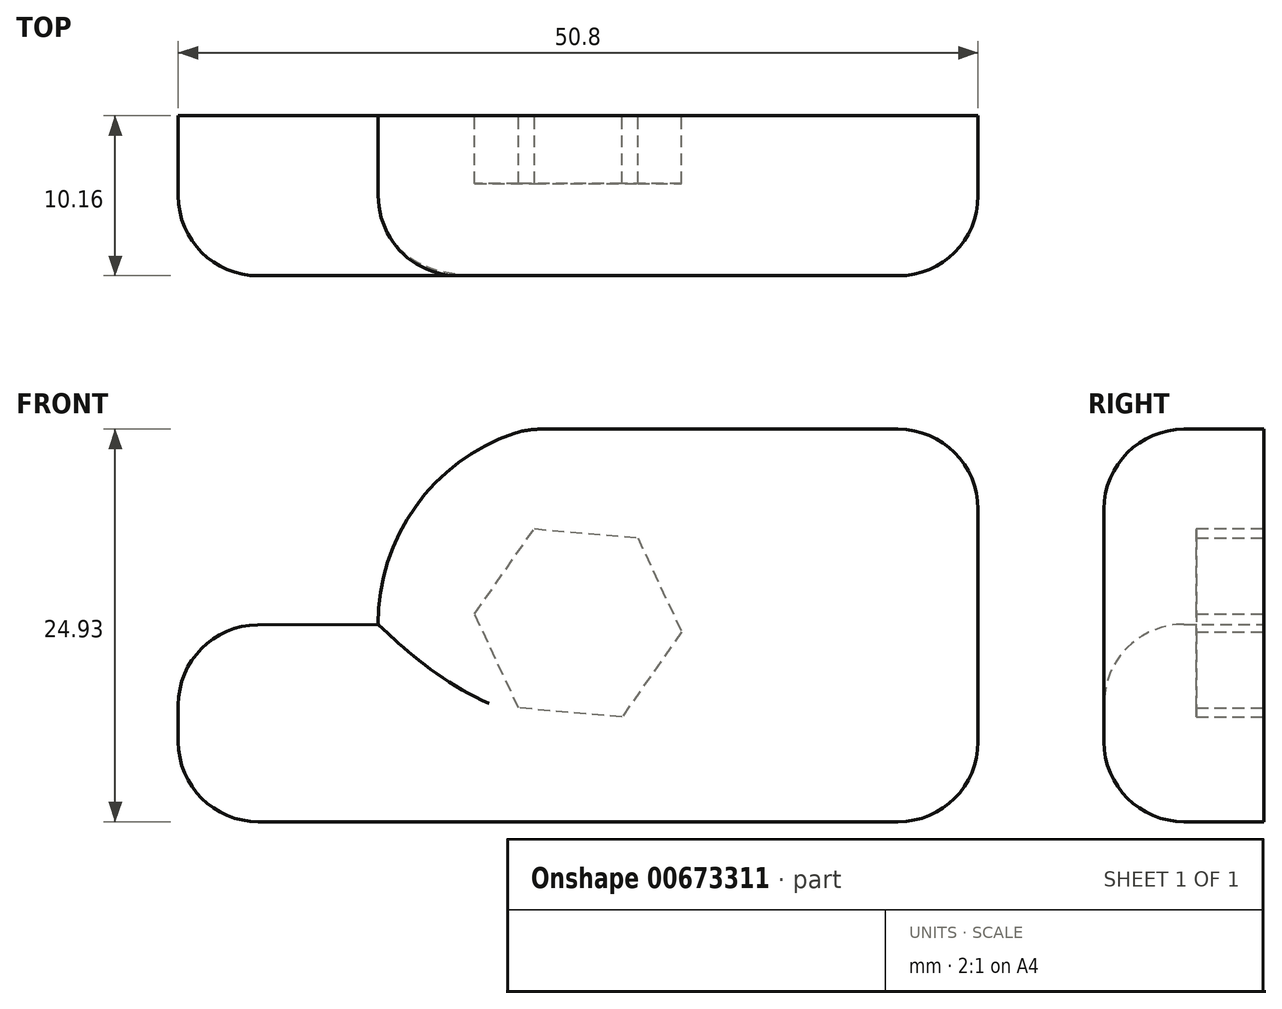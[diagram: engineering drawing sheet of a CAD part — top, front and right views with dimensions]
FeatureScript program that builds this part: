
annotation { "Feature Type Name" : "Feature", "Feature Type Description" : "" }
export const myFeature = defineFeature(function(context is Context, id is Id, definition is map)
    precondition{}
    {
        {
            var Q0;
            Q0=qCreatedBy(makeId("Front.planeOp"),FACE);
            var sketch = newSketch(context, id + "F0", { "sketchPlane" : qUnion([Q0])});
            skCircle(sketch, "E0.cCircle", {"center": v(0, 0) * mm, "radius": 5.72 * mm, "construction": true});
            skLineSegment(sketch, "E0.0", {"start": v(3.79, 5.4) * mm, "end": v(6.57, -0.58) * mm});
            skLineSegment(sketch, "E0.1", {"start": v(6.57, -0.58) * mm, "end": v(2.79, -5.98) * mm});
            skLineSegment(sketch, "E0.2", {"start": v(2.79, -5.98) * mm, "end": v(-3.79, -5.4) * mm});
            skLineSegment(sketch, "E0.3", {"start": v(-3.79, -5.4) * mm, "end": v(-6.57, 0.58) * mm});
            skLineSegment(sketch, "E0.4", {"start": v(-6.57, 0.58) * mm, "end": v(-2.79, 5.98) * mm});
            skLineSegment(sketch, "E0.5", {"start": v(-2.79, 5.98) * mm, "end": v(3.79, 5.4) * mm});
            skPoint(sketch, "E0.0.midPoint", {"position": v(5.18, 2.41) * mm});
            skCircle(sketch, "E1", {"center": v(0, 0) * mm, "radius": 12.7 * mm});
            skLineSegment(sketch, "E2.bottom", {"start": v(-25.4, 12.3) * mm, "end": v(25.4, 12.3) * mm});
            skLineSegment(sketch, "E2.top", {"start": v(-25.4, -12.63) * mm, "end": v(25.4, -12.63) * mm});
            skLineSegment(sketch, "E2.left", {"start": v(-25.4, 12.3) * mm, "end": v(-25.4, -12.63) * mm});
            skLineSegment(sketch, "E2.right", {"start": v(25.4, 12.3) * mm, "end": v(25.4, -12.63) * mm});
            skLineSegment(sketch, "E3", {"start": v(-25.4, -0.17) * mm, "end": v(0, 0) * mm});
            skSolve(sketch);
        }
        {
            var Q0;
            {var subQ0=sQuery(id+"F0.wireOp",EDGE,"E3");var subQ1=sQuery(id+"F0.wireOp",EDGE,"E1");var subQ2=makeQuery(id+"F0.imprint","INTERSECT",VERTEX,{"derivedFrom":[subQ1,subQ0]});Q0=makeQuery(id+"F0.imprint","IMPRINT",FACE,{"disambiguationData":[TD([[makeQuery(id+"F0.imprint","IMPRINT",EDGE,{"disambiguationData":[TD([[subQ2,-1.0]])],"derivedFrom":subQ1}),-1.0]])]});}
            var Q1;
            {var subQ0=sQuery(id+"F0.wireOp",EDGE,"E2.bottom");var subQ1=sQuery(id+"F0.wireOp",EDGE,"E1");var subQ2=makeQuery(id+"F0.imprint","INTERSECT",VERTEX,{"disambiguationData":[OD(0.0)],"derivedFrom":[subQ1,subQ0]});Q1=makeQuery(id+"F0.imprint","IMPRINT",FACE,{"disambiguationData":[TD([[makeQuery(id+"F0.imprint","IMPRINT",EDGE,{"disambiguationData":[TD([[subQ2,-1.0]])],"derivedFrom":subQ1}),-1.0]])]});}
            var Q2;
            {var subQ5=sQuery(id+"F0.wireOp",EDGE,"E2.right");Q2=makeQuery(id+"F0.imprint","IMPRINT",FACE,{"disambiguationData":[TD([[makeQuery(id+"F0.imprint","IMPRINT",EDGE,{"derivedFrom":subQ5}),-1.0]])]});}
            var Q3;
            Q3=makeQuery(id+"F0.imprint","IMPRINT",FACE,{"disambiguationData":[TD([[makeQuery(id+"F0.imprint","IMPRINT",EDGE,{"derivedFrom":sQuery(id+"F0.wireOp",EDGE,"E0.0")}),1.0]])]});
            var Q4;
            Q4=makeQuery(id+"F0.imprint","IMPRINT",FACE,{"disambiguationData":[TD([[makeQuery(id+"F0.imprint","IMPRINT",EDGE,{"derivedFrom":sQuery(id+"F0.wireOp",EDGE,"E0.0")}),-1.0]])]});
            var Q5;
            {var subQ0=sQuery(id+"F0.wireOp",EDGE,"E2.top");var subQ1=sQuery(id+"F0.wireOp",EDGE,"E1");var subQ2=makeQuery(id+"F0.imprint","INTERSECT",VERTEX,{"disambiguationData":[OD(0.0)],"derivedFrom":[subQ1,subQ0]});Q5=makeQuery(id+"F0.imprint","IMPRINT",FACE,{"disambiguationData":[TD([[makeQuery(id+"F0.imprint","IMPRINT",EDGE,{"disambiguationData":[TD([[subQ2,-1.0]])],"derivedFrom":subQ1}),1.0]])]});}
            var Q6;
            {var subQ0=sQuery(id+"F0.wireOp",EDGE,"E2.bottom");var subQ1=sQuery(id+"F0.wireOp",EDGE,"E1");var subQ2=makeQuery(id+"F0.imprint","INTERSECT",VERTEX,{"disambiguationData":[OD(0.0)],"derivedFrom":[subQ1,subQ0]});Q6=makeQuery(id+"F0.imprint","IMPRINT",FACE,{"disambiguationData":[TD([[makeQuery(id+"F0.imprint","IMPRINT",EDGE,{"disambiguationData":[TD([[subQ2,1.0]])],"derivedFrom":subQ1}),1.0]])]});}
            extrude(context, id + "F1", {"entities" : qUnion([Q0, Q1, Q2, Q3, Q4, Q5, Q6]), "depth" : 10.16 * mm, "offsetDistance" : 25.4 * mm});
        }
        {
            var Q0;
            Q0=makeQuery(id+"F0.imprint","IMPRINT",FACE,{"disambiguationData":[TD([[makeQuery(id+"F0.imprint","IMPRINT",EDGE,{"derivedFrom":sQuery(id+"F0.wireOp",EDGE,"E0.0")}),-1.0]])]});
            extrude(context, id + "F2", {"entities" : qUnion([Q0]), "operationType" : NewBodyOperationType.REMOVE, "depth" : 4.3 * mm, "offsetDistance" : 25.4 * mm});
        }
        {
            var Q0;
            Q0=makeQuery(id+"F1.opExtrude","SWEPT_EDGE",EDGE,{"disambiguationData":[OSD([sQuery(id+"F0.wireOp",EDGE,"E2.bottom"),sQuery(id+"F0.wireOp",EDGE,"E2.left")])]});
            var Q1;
            Q1=makeQuery(id+"F1.opExtrude","SWEPT_EDGE",EDGE,{"disambiguationData":[OSD([sQuery(id+"F0.wireOp",EDGE,"E2.bottom"),sQuery(id+"F0.wireOp",EDGE,"E2.right")])]});
            var Q2;
            Q2=makeQuery(id+"F1.opExtrude","SWEPT_EDGE",EDGE,{"disambiguationData":[OSD([sQuery(id+"F0.wireOp",EDGE,"E2.top"),sQuery(id+"F0.wireOp",EDGE,"E2.right")])]});
            var Q3;
            {var subQ0=sQuery(id+"F0.wireOp",EDGE,"E2.top");Q3=makeQuery(id+"F1.opExtrude","CAP_EDGE",EDGE,{"disambiguationData":[OSD([subQ0]),TDD([makeQuery(id+"F0.imprint","IMPRINT",EDGE,{"disambiguationData":[TD([[makeQuery(id+"F0.imprint","INTERSECT",VERTEX,{"derivedFrom":[subQ0,sQuery(id+"F0.wireOp",EDGE,"E2.right")]}),1.0]])],"derivedFrom":subQ0})])],"isStart":false});}
            var Q4;
            Q4=makeQuery(id+"F1.opExtrude","CAP_FACE",FACE,{"disambiguationData":[OSD([sQuery(id+"F0.wireOp",EDGE,"E1"),sQuery(id+"F0.wireOp",EDGE,"E2.bottom"),sQuery(id+"F0.wireOp",EDGE,"E2.top"),sQuery(id+"F0.wireOp",EDGE,"E2.left"),sQuery(id+"F0.wireOp",EDGE,"E2.right")])],"isStart":false});
            var Q5;
            Q5=makeQuery(id+"F1.opExtrude","SWEPT_EDGE",EDGE,{"disambiguationData":[OSD([sQuery(id+"F0.wireOp",EDGE,"E2.top"),sQuery(id+"F0.wireOp",EDGE,"E2.left")])]});
            fillet(context, id + "F3", {"entities" : qUnion([Q0, Q1, Q2, Q3, Q4, Q5]), "radius" : 5.08 * mm, "tangentPropagation" : true, "allowEdgeOverflow" : false});
        }
    });
